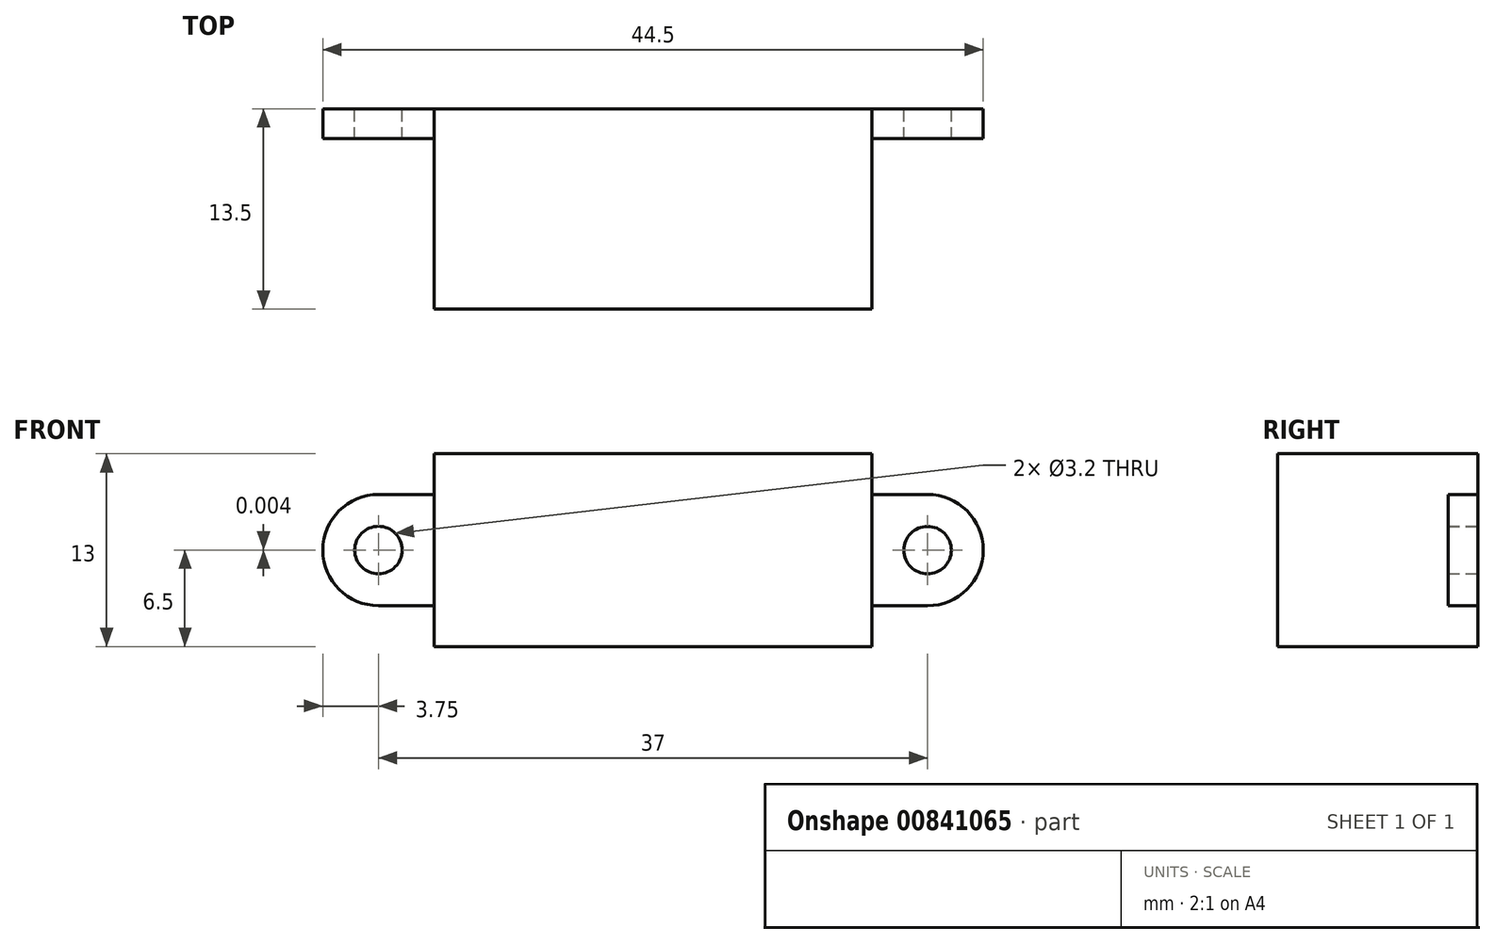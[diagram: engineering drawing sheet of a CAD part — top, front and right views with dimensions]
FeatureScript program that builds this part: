
annotation { "Feature Type Name" : "Feature", "Feature Type Description" : "" }
export const myFeature = defineFeature(function(context is Context, id is Id, definition is map)
    precondition{}
    {
        {
            var Q0;
            Q0=qCreatedBy(makeId("Front.planeOp"),FACE);
            var sketch = newSketch(context, id + "F0", { "sketchPlane" : qUnion([Q0])});
            skLineSegment(sketch, "E0.bottom", {"start": v(-27.27, 13) * mm, "end": v(2.23, 13) * mm});
            skLineSegment(sketch, "E0.top", {"start": v(-27.27, 0) * mm, "end": v(2.23, 0) * mm});
            skLineSegment(sketch, "E0.left", {"start": v(-27.27, 13) * mm, "end": v(-27.27, 0) * mm});
            skLineSegment(sketch, "E0.right", {"start": v(2.23, 13) * mm, "end": v(2.23, 0) * mm});
            skLineSegment(sketch, "E1.top", {"start": v(-27.27, 0) * mm, "end": v(-34.27, 0) * mm});
            skCircle(sketch, "E2", {"center": v(-31.02, 6.5) * mm, "radius": 1.6 * mm});
            skCircle(sketch, "E3", {"center": v(5.98, 6.5) * mm, "radius": 1.6 * mm});
            skPoint(sketch, "E3.centerSnap0", {"position": v(2.23, 6.5) * mm});
            skLineSegment(sketch, "E4.bottom", {"start": v(-27.27, 10.25) * mm, "end": v(-34.77, 10.25) * mm});
            skLineSegment(sketch, "E4.top", {"start": v(-27.27, 2.75) * mm, "end": v(-34.77, 2.75) * mm});
            skLineSegment(sketch, "E4.left", {"start": v(-27.27, 10.25) * mm, "end": v(-27.27, 2.75) * mm});
            skLineSegment(sketch, "E4.right", {"start": v(-34.77, 10.25) * mm, "end": v(-34.77, 2.75) * mm});
            skLineSegment(sketch, "E5.right", {"start": v(9.73, 10.25) * mm, "end": v(9.73, 2.75) * mm});
            skLineSegment(sketch, "E6", {"start": v(-31.02, 6.5) * mm, "end": v(-34.77, 6.5) * mm});
            skLineSegment(sketch, "E7", {"start": v(-34.77, 6.5) * mm, "end": v(-31.02, 6.5) * mm});
            skLineSegment(sketch, "E8", {"start": v(-31.02, 10.25) * mm, "end": v(-31.02, 6.5) * mm});
            skLineSegment(sketch, "E9", {"start": v(9.73, 10.25) * mm, "end": v(2.23, 10.25) * mm});
            skLineSegment(sketch, "E10", {"start": v(9.73, 2.75) * mm, "end": v(2.23, 2.75) * mm});
            skLineSegment(sketch, "E11", {"start": v(2.23, 10.25) * mm, "end": v(2.23, 2.75) * mm});
            skLineSegment(sketch, "E12", {"start": v(5.98, 6.5) * mm, "end": v(9.73, 6.5) * mm});
            skLineSegment(sketch, "E13", {"start": v(9.73, 6.5) * mm, "end": v(5.98, 6.5) * mm});
            skLineSegment(sketch, "E14", {"start": v(5.98, 2.75) * mm, "end": v(5.98, 6.5) * mm});
            skSolve(sketch);
        }
        {
            var Q0;
            Q0=makeQuery(id+"F0.imprint","IMPRINT",FACE,{"disambiguationData":[TD([[makeQuery(id+"F0.imprint","IMPRINT",EDGE,{"derivedFrom":sQuery(id+"F0.wireOp",EDGE,"E0.bottom")}),-1.0]])]});
            extrude(context, id + "F1", {"entities" : qUnion([Q0]), "depth" : 13.5 * mm, "offsetDistance" : 25 * mm});
        }
        {
            var Q0;
            {var subQ1=sQuery(id+"F0.wireOp",EDGE,"E4.bottom");Q0=makeQuery(id+"F0.imprint","IMPRINT",FACE,{"disambiguationData":[TD([[makeQuery(id+"F0.imprint","IMPRINT",EDGE,{"derivedFrom":subQ1}),1.0]])]});}
            var Q1;
            {var subQ1=sQuery(id+"F0.wireOp",EDGE,"E4.top");Q1=makeQuery(id+"F0.imprint","IMPRINT",FACE,{"disambiguationData":[TD([[makeQuery(id+"F0.imprint","IMPRINT",EDGE,{"derivedFrom":subQ1}),-1.0]])]});}
            var Q2;
            {var subQ1=sQuery(id+"F0.wireOp",EDGE,"E5.bottom");Q2=makeQuery(id+"F0.imprint","IMPRINT",FACE,{"disambiguationData":[TD([[makeQuery(id+"F0.imprint","IMPRINT",EDGE,{"derivedFrom":subQ1}),-1.0]])]});}
            var Q3;
            {var subQ1=sQuery(id+"F0.wireOp",EDGE,"E5.top");Q3=makeQuery(id+"F0.imprint","IMPRINT",FACE,{"disambiguationData":[TD([[makeQuery(id+"F0.imprint","IMPRINT",EDGE,{"derivedFrom":subQ1}),1.0]])]});}
            extrude(context, id + "F2", {"entities" : qUnion([Q0, Q1, Q2, Q3]), "operationType" : NewBodyOperationType.ADD, "depth" : 2 * mm, "offsetDistance" : 25 * mm});
        }
        {
            var Q0;
            Q0=makeQuery(id+"F2.opExtrude","SWEPT_EDGE",EDGE,{"disambiguationData":[OSD([sQuery(id+"F0.wireOp",EDGE,"E4.bottom"),sQuery(id+"F0.wireOp",EDGE,"E4.right")])]});
            var Q1;
            Q1=makeQuery(id+"F2.opExtrude","SWEPT_EDGE",EDGE,{"disambiguationData":[OSD([sQuery(id+"F0.wireOp",EDGE,"E4.top"),sQuery(id+"F0.wireOp",EDGE,"E4.right")])]});
            fillet(context, id + "F3", {"entities" : qUnion([Q0, Q1]), "radius" : 3.75 * mm, "tangentPropagation" : true, "allowEdgeOverflow" : false});
        }
        {
            var Q0;
            {var subQ4=sQuery(id+"F0.wireOp",EDGE,"E9");Q0=makeQuery(id+"F0.imprint","IMPRINT",FACE,{"disambiguationData":[TD([[makeQuery(id+"F0.imprint","IMPRINT",EDGE,{"derivedFrom":subQ4}),1.0]])]});}
            var Q1;
            {var subQ0=sQuery(id+"F0.wireOp",EDGE,"E13");var subQ3=sQuery(id+"F0.wireOp",EDGE,"E3");var subQ4=makeQuery(id+"F0.imprint","INTERSECT",VERTEX,{"derivedFrom":[subQ3,subQ0]});Q1=makeQuery(id+"F0.imprint","IMPRINT",FACE,{"disambiguationData":[TD([[makeQuery(id+"F0.imprint","IMPRINT",EDGE,{"disambiguationData":[TD([[subQ4,1.0]])],"derivedFrom":subQ3}),-1.0]])]});}
            extrude(context, id + "F4", {"entities" : qUnion([Q0, Q1]), "operationType" : NewBodyOperationType.ADD, "depth" : 2 * mm, "offsetDistance" : 25 * mm});
        }
        {
            var Q0;
            Q0=makeQuery(id+"F4.opExtrude","SWEPT_EDGE",EDGE,{"disambiguationData":[OSD([sQuery(id+"F0.wireOp",EDGE,"E5.right"),sQuery(id+"F0.wireOp",EDGE,"E9")])]});
            var Q1;
            Q1=makeQuery(id+"F4.opExtrude","SWEPT_EDGE",EDGE,{"disambiguationData":[OSD([sQuery(id+"F0.wireOp",EDGE,"E5.right"),sQuery(id+"F0.wireOp",EDGE,"E10")])]});
            fillet(context, id + "F5", {"entities" : qUnion([Q0, Q1]), "radius" : 3.75 * mm, "tangentPropagation" : true, "allowEdgeOverflow" : false});
        }
    });
